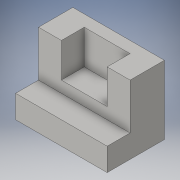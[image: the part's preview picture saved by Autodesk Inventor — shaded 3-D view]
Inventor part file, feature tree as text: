
AUTODESK INVENTOR PART (.ipt)
format: ipt  version: 2016 (Build 200138000, 138)  size: 109,056 bytes
history: native  units: in
note: dims shown in document units (in); Inventor stores cm internally (conversion verified against a paired STEP export)
features: extrude x3, sketch x3
ambient origin geometry x8: Origin, YZ Plane, XZ Plane, XY Plane, X Axis, Y Axis, Z Axis, Center Point
bodies: Solid1 (feature_tree)
feature tree (6):
  extrude  "Extrusion1"  Depth=1.5in
  extrude  "Extrusion2"  Depth=0.5in
  extrude  "Extrusion3"  Depth=1.0in
  sketch  "Sketch1"  dims[d0=2.0in d1=1.5in]
  sketch  "Sketch2"  dims[d2=1.25in d3=0.0in d4=0.5in]
  sketch  "Sketch3"  dims[d5=0.5in d6=0.0in d7=1.0in d8=0.5in d9=0.75in d10=0.5in d11=0.0in]
